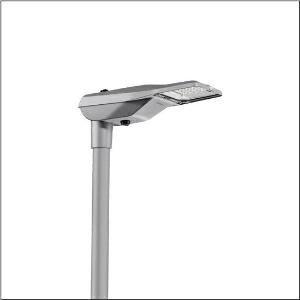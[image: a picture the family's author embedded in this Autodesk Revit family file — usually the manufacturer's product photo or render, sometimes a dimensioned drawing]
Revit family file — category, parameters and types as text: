
# Revit family: streetlight_sl_21_iq_micro___st1_0a_5xe1d21y08cb_9119
name_source: partatom
category: Lighting Fixtures
units: mm (PartAtom-declared; Revit-internal decimal feet)

## family parameters
Cut with Voids When Loaded = No
Host = Face
Light Source = No
Part Type = Normal
Room Calculation Point = No
Round Connector Dimension = Use Diameter
Shared = No

## types (1)
- --- (1 x LED, 2310 lm, 19.1 W, 2200K)
    Apparent Load = 19 VA
    CIE Flux Codes = 37 72 97 100 100
    Color Rendering = 70
    Color Temperature = 2200K
    Default Elevation = 1800 mm
    Description = Streetlight SL 21 iQ micro, mast luminaire, primary light control with lens, of PMMA, primary optical cover: cover, of toughened safety glass, transparent, light distribution: ST1.0a, light emission: direct distribution, primary light characteristic: asymmetric, installation type: post-top, side-entry, LED, High Power LED, rated luminous flux: 2.310lm, luminous efficacy: 121lm/W, light colour: 722, colour temperature: 2200K, control: presetting dimming logarithmic, Street-Remote, Auto-Match, Temp-Guard, Lumen-Switch, Night-Set, Smart-Wire, Light-Fading, Desk-Remote (wireless, voltage-free reading and setting of iQ features in the workshop via application-optimized NFC function/RFID function), optimised constant luminous flux control (CLO 2.0), mains connection: 220..240V, AC, 50/60Hz, start of lifetime: 19W, end of service life: 20W, reduction: 9W, luminaire housing, of diecast aluminium, powder-coated, Siteco® metallic grey (DB 702S), corrosivity category C5 mid according to DIN EN ISO 12944, please order mast flange separately, inclination adjustable: 0°, 5°, 10°, 15°, sealing non-destructively replaceable, multi-level sealing system, length: 528mm, width: 235mm, height: 110mm, mast flange for spigot size: 42mm (side-entry): 5XC10008XM4, 60/48mm (side-entry/post-top): 5XC10108XM2, 76/60mm (side-entry/post-top): 5XC10108XM1, Smart Interface below and above, protection rating (complete): IP66, insulation class (complete): insulation class II (safety insulation), certification: CE, ENEC, ENEC+, VDE, impact resistance: IK09, permissible operating ambient temperature for outdoor applications: -40..+50°C, standard-compliant lighting for roads and squares, packaging unit: 1 piece

Light Distribution: ST1.0a
    Height = 110 mm
    Lamp = 1 x LED
    Lamp Light Flux = 2310 lm
    Lamp Power = 19.1 W
    Lamp count = 1
    Length = 528 mm
    Luminous efficacy = 121 lm/W
    Manufacturer = Siteco
    ModVariant = No
    Model = 5XE1D21Y08CB
    Number of Poles = 1
    OnlyDefault = Yes
    Power Factor = 1
    Product Name = Streetlight SL 21 iQ micro | ST1.0a
    Product group = mast luminaire | pylon top
    ProductGroupID = 6100
    Protection Class = Protection class II
    Protection Degree = IP 66
    RLX_Detail_Level = 1
    RLX_Emergency_Light_Flux = 0 lm
    RLX_Emergency_Type = 0
    RLX_Emergency_Type_DB = No
    RlxData = <blob elided: 98861 chars, md5=a94ebedf>
    Socket = socket
    Standby Power = 0 W
    System Light Flux = 2310 lm
    System Power = 19 W
    Type Comments = factory setting: luminous flux: 100 % | dim-lin: 254 | 387 mA
    Type Image = l_1007239.jpg
    URL = http://relux.com
    VarID = @adj_045647
    Voltage = 0 V
    Weight = 0.00 kg
    Width = 235 mm

## geometry (parser evidence)
native form markers: Blend x4, Sweep x11
no freeform markers — native parametric forms only
